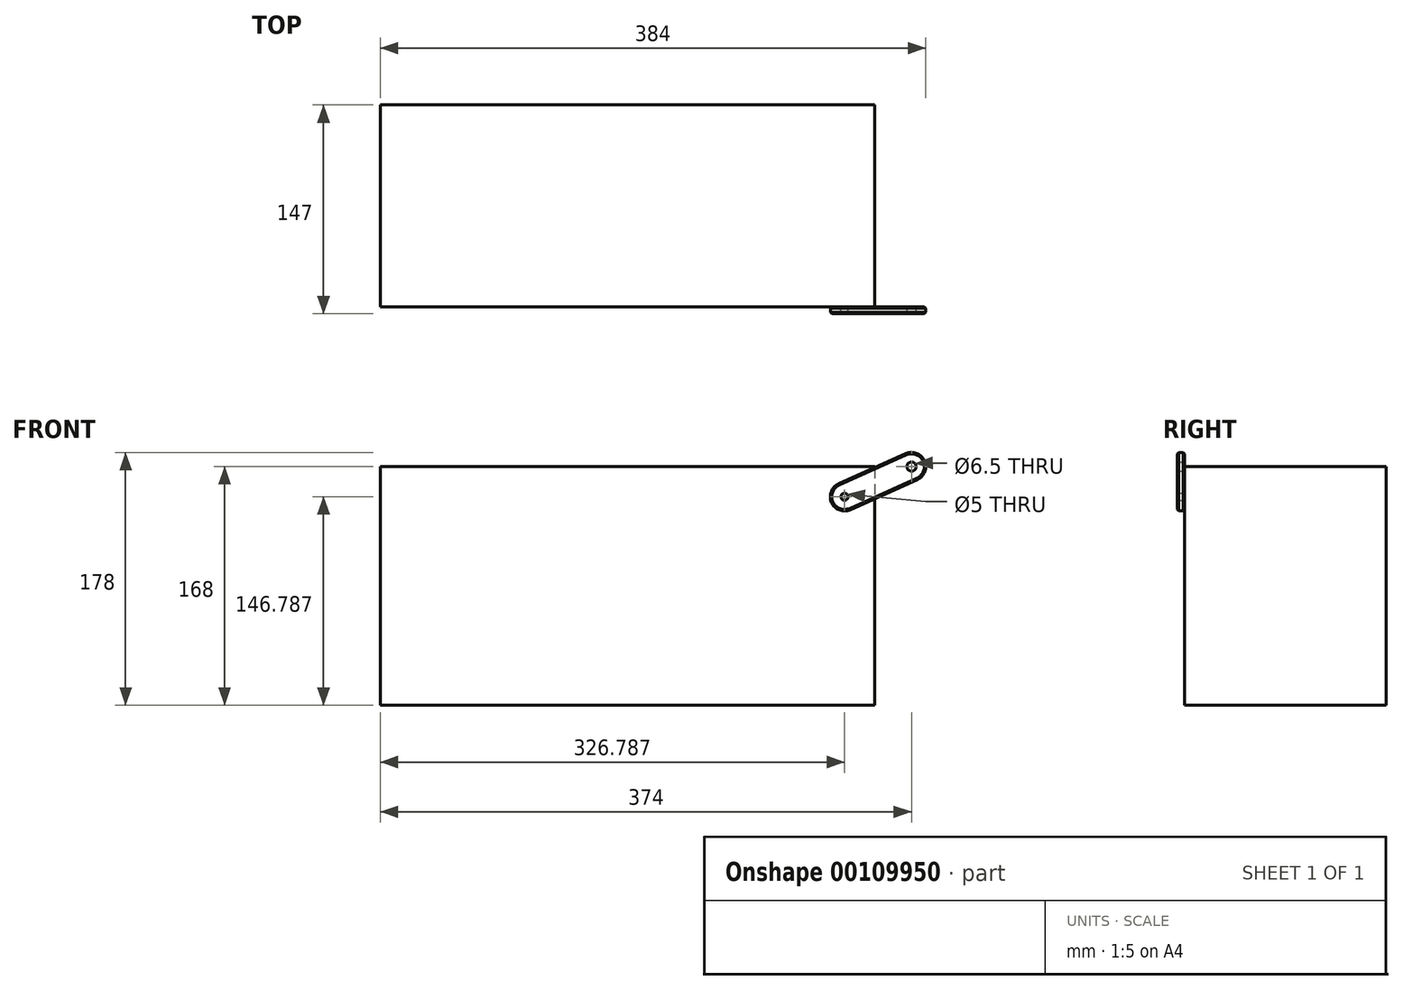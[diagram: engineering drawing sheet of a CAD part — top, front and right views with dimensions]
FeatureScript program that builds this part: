
annotation { "Feature Type Name" : "Feature", "Feature Type Description" : "" }
export const myFeature = defineFeature(function(context is Context, id is Id, definition is map)
    precondition{}
    {
        {
            var Q0;
            Q0=qCreatedBy(makeId("Front.planeOp"),FACE);
            var sketch = newSketch(context, id + "F0", { "sketchPlane" : qUnion([Q0])});
            skLineSegment(sketch, "E0.bottom", {"start": v(174, 84) * mm, "end": v(-174, 84) * mm});
            skLineSegment(sketch, "E0.top", {"start": v(174, -84) * mm, "end": v(-174, -84) * mm});
            skLineSegment(sketch, "E0.left", {"start": v(174, 84) * mm, "end": v(174, -84) * mm});
            skLineSegment(sketch, "E0.right", {"start": v(-174, 84) * mm, "end": v(-174, -84) * mm});
            skPoint(sketch, "E0.middle", {"position": v(0, 0) * mm});
            skLineSegment(sketch, "E1", {"start": v(174, 84) * mm, "end": v(200, 84) * mm, "construction": true});
            skLineSegment(sketch, "E2", {"start": v(-174, 84) * mm, "end": v(-200, 84) * mm, "construction": true});
            skSolve(sketch);
        }
        {
            var Q0;
            Q0=makeQuery(id+"F0.imprint","IMPRINT",FACE,{"disambiguationData":[TD([[makeQuery(id+"F0.imprint","IMPRINT",EDGE,{"derivedFrom":sQuery(id+"F0.wireOp",EDGE,"E0.bottom")}),1.0]])]});
            extrude(context, id + "F1", {"entities" : qUnion([Q0]), "oppositeDirection" : true, "depth" : 142 * mm});
        }
        {
            var Q0;
            Q0=makeQuery(id+"F0.imprint","IMPRINT",FACE,{"disambiguationData":[TD([[makeQuery(id+"F0.imprint","IMPRINT",EDGE,{"derivedFrom":sQuery(id+"F0.wireOp",EDGE,"E0.bottom")}),1.0]])]});
            var sketch = newSketch(context, id + "F2", { "sketchPlane" : qUnion([Q0])});
            skPoint(sketch, "E3.0", {"position": v(200, 84) * mm});
            skPoint(sketch, "E4.0", {"position": v(-200, 84) * mm});
            skArc(sketch, "E5", {"start": v(204.1, 74.88) * mm, "mid": v(209.12, 88.1) * mm, "end": v(195.9, 93.12) * mm});
            skLineSegment(sketch, "E6.0", {"start": v(174, 84) * mm, "end": v(-174, 84) * mm});
            skLineSegment(sketch, "E7.0", {"start": v(174, 84) * mm, "end": v(174, -84) * mm});
            skLineSegment(sketch, "E8.0", {"start": v(-174, 84) * mm, "end": v(-174, -84) * mm});
            skLineSegment(sketch, "E9", {"start": v(174, 84) * mm, "end": v(152.79, 62.79) * mm, "construction": true});
            skArc(sketch, "E10", {"start": v(148.69, 71.9) * mm, "mid": v(143.67, 58.69) * mm, "end": v(156.89, 53.67) * mm});
            skLineSegment(sketch, "E11", {"start": v(195.9, 93.12) * mm, "end": v(148.69, 71.9) * mm});
            skLineSegment(sketch, "E12", {"start": v(156.89, 53.67) * mm, "end": v(204.1, 74.88) * mm});
            skCircle(sketch, "E13", {"center": v(200, 84) * mm, "radius": 3.25 * mm});
            skCircle(sketch, "E14", {"center": v(152.79, 62.79) * mm, "radius": 2.5 * mm});
            skSolve(sketch);
        }
        {
            var Q0;
            {var subQ1=sQuery(id+"F2.wireOp",EDGE,"E5");Q0=makeQuery(id+"F2.imprint","IMPRINT",FACE,{"disambiguationData":[TD([[makeQuery(id+"F2.imprint","IMPRINT",EDGE,{"derivedFrom":subQ1}),1.0]])]});}
            var Q1;
            {var subQ0=sQuery(id+"F2.wireOp",EDGE,"E10");Q1=makeQuery(id+"F2.imprint","IMPRINT",FACE,{"disambiguationData":[TD([[makeQuery(id+"F2.imprint","IMPRINT",EDGE,{"derivedFrom":subQ0}),1.0]])]});}
            extrude(context, id + "F3", {"entities" : qUnion([Q0, Q1]), "depth" : 5 * mm});
        }
        {
            var Q0;
            Q0=makeQuery(id+"F3.opExtrude","CAP_EDGE",EDGE,{"disambiguationData":[OSD([sQuery(id+"F2.wireOp",EDGE,"E11")])],"isStart":false});
            var Q1;
            Q1=makeQuery(id+"F3.opExtrude","CAP_EDGE",EDGE,{"disambiguationData":[OSD([sQuery(id+"F2.wireOp",EDGE,"E11")])],"isStart":true});
            chamfer(context, id + "F4", {"entities" : qUnion([Q0, Q1]), "width" : 1 * mm, "tangentPropagation" : true});
        }
    });
